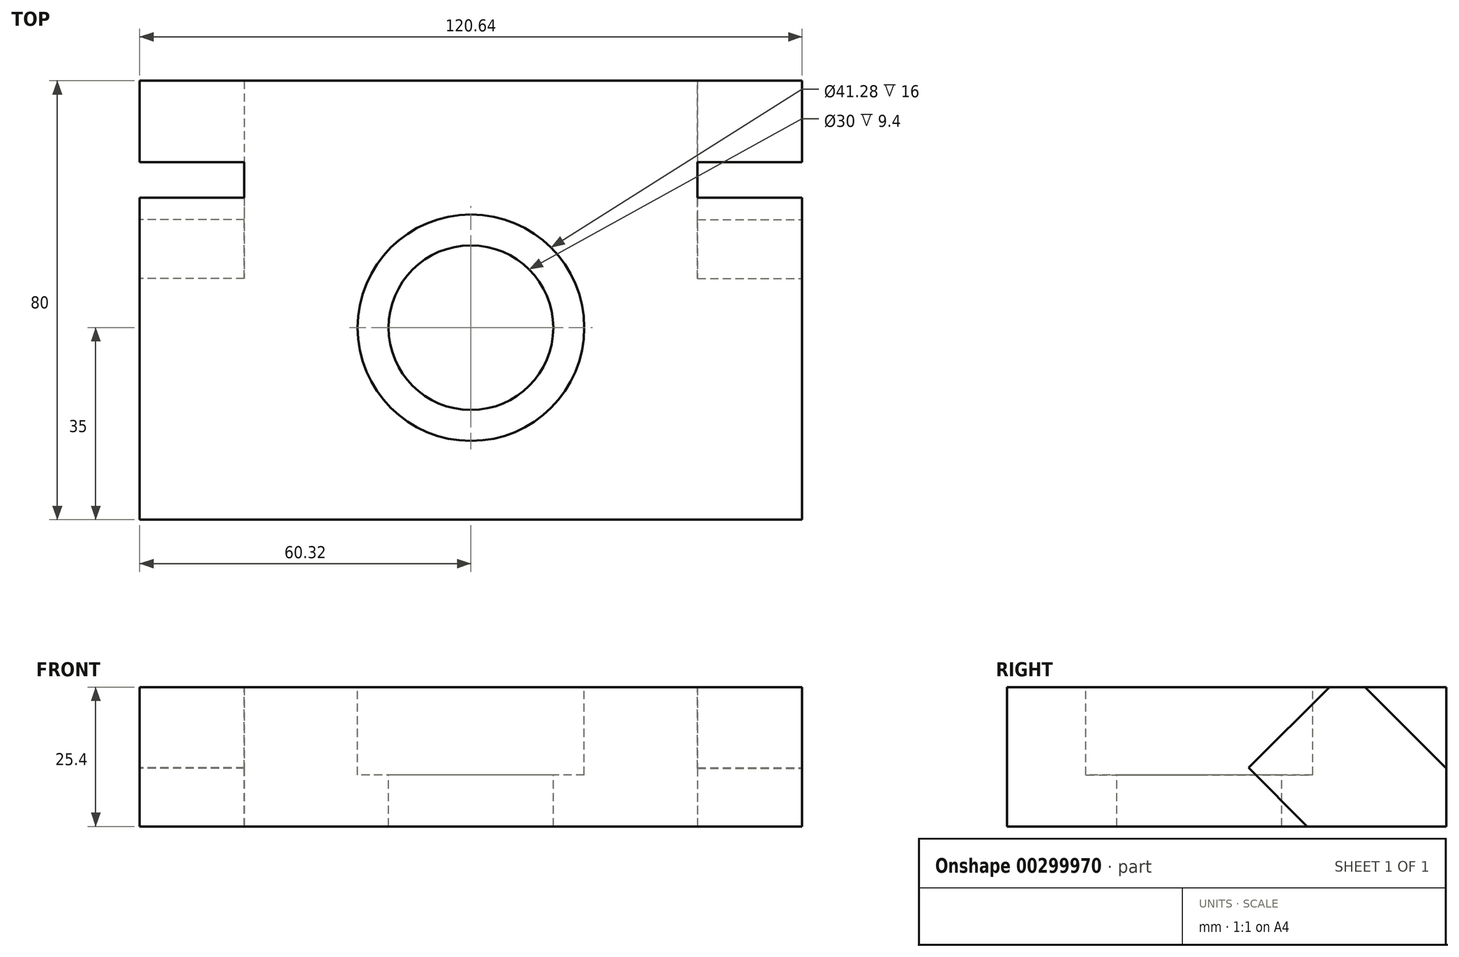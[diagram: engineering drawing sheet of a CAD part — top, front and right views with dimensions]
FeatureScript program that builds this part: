
annotation { "Feature Type Name" : "Feature", "Feature Type Description" : "" }
export const myFeature = defineFeature(function(context is Context, id is Id, definition is map)
    precondition{}
    {
        {
            var Q0;
            Q0=qCreatedBy(makeId("Top.planeOp"),FACE);
            var sketch = newSketch(context, id + "F0", { "sketchPlane" : qUnion([Q0])});
            skLineSegment(sketch, "E0.bottom", {"start": v(-60.33, 40) * mm, "end": v(60.33, 40) * mm});
            skLineSegment(sketch, "E0.top", {"start": v(-60.33, -40) * mm, "end": v(60.33, -40) * mm});
            skLineSegment(sketch, "E0.left", {"start": v(-60.33, 40) * mm, "end": v(-60.33, -40) * mm});
            skLineSegment(sketch, "E0.right", {"start": v(60.33, 40) * mm, "end": v(60.33, -40) * mm});
            skSolve(sketch);
        }
        {
            var Q0;
            Q0 = qSketchRegion(id + "F0", true);
            extrude(context, id + "F1", {"entities" : qUnion([Q0]), "depth" : 25.4 * mm, "offsetDistance" : 25 * mm});
        }
        {
            var Q0;
            Q0=makeQuery(id+"F1.opExtrude","SWEPT_FACE",FACE,{"disambiguationData":[OSD([sQuery(id+"F0.wireOp",EDGE,"E0.right")])]});
            var sketch = newSketch(context, id + "F2", { "sketchPlane" : qUnion([Q0])});
            skLineSegment(sketch, "E1", {"start": v(4, 10.69) * mm, "end": v(39.35, -24.67) * mm});
            skLineSegment(sketch, "E2", {"start": v(39.35, -24.67) * mm, "end": v(57.3, -6.7) * mm});
            skLineSegment(sketch, "E3", {"start": v(57.3, -6.7) * mm, "end": v(21.95, 28.65) * mm});
            skLineSegment(sketch, "E4", {"start": v(21.95, 28.65) * mm, "end": v(4, 10.69) * mm});
            skLineSegment(sketch, "E5.bottom", {"start": v(39.35, -24.67) * mm, "end": v(2.09, -24.67) * mm});
            skLineSegment(sketch, "E5.top", {"start": v(39.35, -24.67) * mm, "end": v(2.09, -24.67) * mm});
            skLineSegment(sketch, "E5.left", {"start": v(39.35, -24.67) * mm, "end": v(39.35, -24.67) * mm});
            skLineSegment(sketch, "E5.right", {"start": v(2.09, -24.67) * mm, "end": v(2.09, -24.67) * mm});
            skSolve(sketch);
        }
        {
            var Q0;
            Q0 = qSketchRegion(id + "F2", true);
            extrude(context, id + "F3", {"entities" : qUnion([Q0]), "operationType" : NewBodyOperationType.REMOVE, "oppositeDirection" : true, "depth" : 19.05 * mm, "offsetDistance" : 25 * mm});
        }
        {
            var Q0;
            Q0=makeQuery(id+"F1.opExtrude","CAP_FACE",FACE,{"disambiguationData":[OSD([sQuery(id+"F0.wireOp",EDGE,"E0.bottom"),sQuery(id+"F0.wireOp",EDGE,"E0.top"),sQuery(id+"F0.wireOp",EDGE,"E0.left"),sQuery(id+"F0.wireOp",EDGE,"E0.right")])],"isStart":false});
            var sketch = newSketch(context, id + "F4", { "sketchPlane" : qUnion([Q0])});
            skCircle(sketch, "E6", {"center": v(0, -5) * mm, "radius": 20.64 * mm});
            skSolve(sketch);
        }
        {
            var Q0;
            Q0 = qSketchRegion(id + "F4", true);
            extrude(context, id + "F5", {"entities" : qUnion([Q0]), "operationType" : NewBodyOperationType.REMOVE, "oppositeDirection" : true, "depth" : 16 * mm, "offsetDistance" : 25 * mm});
        }
        {
            var Q0;
            Q0=makeQuery(id+"F1.opExtrude","SWEPT_FACE",FACE,{"disambiguationData":[OSD([sQuery(id+"F0.wireOp",EDGE,"E0.left")])]});
            var sketch = newSketch(context, id + "F6", { "sketchPlane" : qUnion([Q0])});
            skLineSegment(sketch, "E7", {"start": v(-57.3, -6.71) * mm, "end": v(-21.94, 28.65) * mm});
            skLineSegment(sketch, "E8", {"start": v(-21.94, 28.65) * mm, "end": v(-3.98, 10.7) * mm});
            skLineSegment(sketch, "E9", {"start": v(-3.98, 10.7) * mm, "end": v(-39.35, -24.67) * mm});
            skLineSegment(sketch, "E10", {"start": v(-39.35, -24.67) * mm, "end": v(-57.3, -6.71) * mm});
            skLineSegment(sketch, "E11", {"start": v(-39.35, -24.67) * mm, "end": v(-16.8, -24.67) * mm});
            skSolve(sketch);
        }
        {
            var Q0;
            Q0 = qSketchRegion(id + "F6", true);
            extrude(context, id + "F7", {"entities" : qUnion([Q0]), "operationType" : NewBodyOperationType.REMOVE, "oppositeDirection" : true, "depth" : 19.05 * mm, "offsetDistance" : 25.4 * mm});
        }
        {
            var Q0;
            Q0=makeQuery(id+"F1.opExtrude","CAP_FACE",FACE,{"disambiguationData":[OSD([sQuery(id+"F0.wireOp",EDGE,"E0.bottom"),sQuery(id+"F0.wireOp",EDGE,"E0.top"),sQuery(id+"F0.wireOp",EDGE,"E0.left"),sQuery(id+"F0.wireOp",EDGE,"E0.right")])],"isStart":false});
            var sketch = newSketch(context, id + "F8", { "sketchPlane" : qUnion([Q0])});
            skCircle(sketch, "E12", {"center": v(0, -5) * mm, "radius": 15 * mm});
            skSolve(sketch);
        }
        {
            var Q0;
            Q0 = qSketchRegion(id + "F8", true);
            extrude(context, id + "F9", {"entities" : qUnion([Q0]), "operationType" : NewBodyOperationType.REMOVE, "endBound" : BoundingType.THROUGH_ALL, "oppositeDirection" : true, "depth" : 25.4 * mm, "offsetDistance" : 25.4 * mm});
        }
    });
